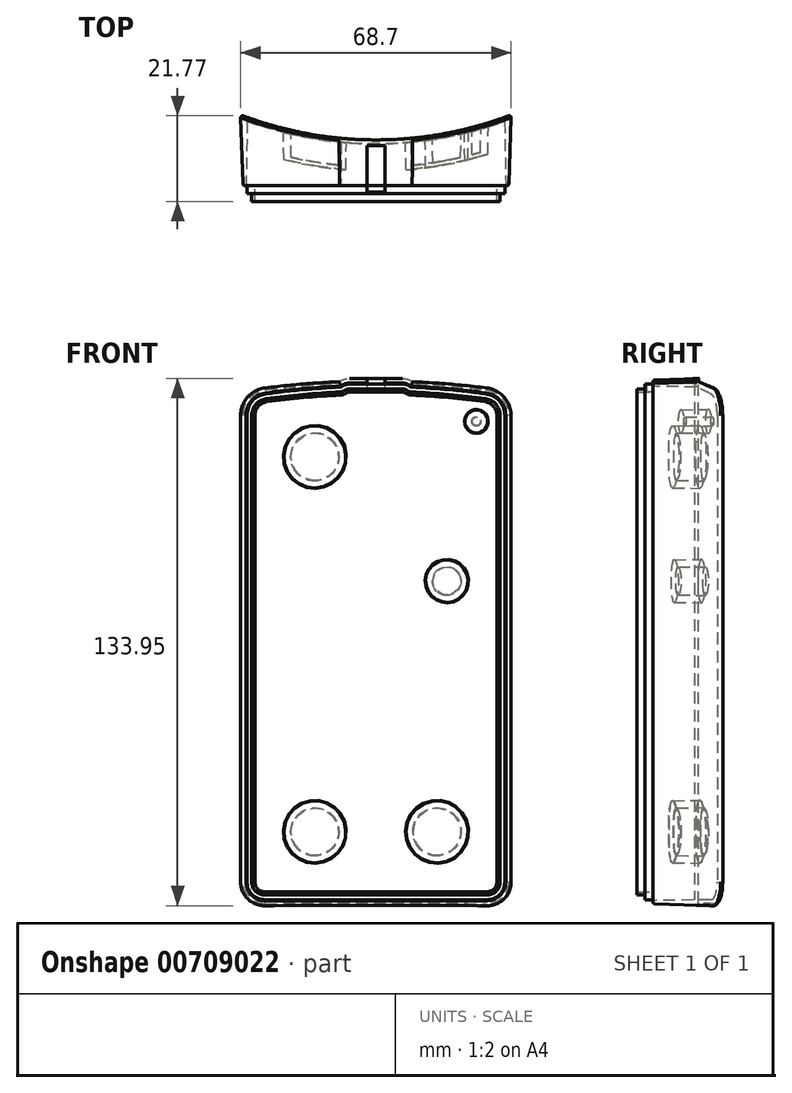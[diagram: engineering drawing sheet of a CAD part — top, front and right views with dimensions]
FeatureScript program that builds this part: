
annotation { "Feature Type Name" : "Feature", "Feature Type Description" : "" }
export const myFeature = defineFeature(function(context is Context, id is Id, definition is map)
    precondition{}
    {
        {
            var Q0;
            Q0=qCreatedBy(makeId("Front.planeOp"),FACE);
            var sketch = newSketch(context, id + "F0", { "sketchPlane" : qUnion([Q0])});
            skLineSegment(sketch, "E0.bottom", {"start": v(4.5, 0) * mm, "end": v(61, 0) * mm});
            skLineSegment(sketch, "E0.left", {"start": v(0, 4.5) * mm, "end": v(0, 123.05) * mm});
            skLineSegment(sketch, "E0.right", {"start": v(65.5, 4.5) * mm, "end": v(65.5, 123.05) * mm});
            skPoint(sketch, "E1.visualSharp", {"position": v(0, 0) * mm});
            skArc(sketch, "E1.filletArc", {"start": v(0, 4.5) * mm, "mid": v(1.32, 1.32) * mm, "end": v(4.5, 0) * mm});
            skPoint(sketch, "E2.visualSharp", {"position": v(65.5, 0) * mm});
            skArc(sketch, "E2.filletArc", {"start": v(61, 0) * mm, "mid": v(64.18, 1.32) * mm, "end": v(65.5, 4.5) * mm});
            skArc(sketch, "E3.filletArc", {"start": v(4.76, 128.5) * mm, "mid": v(1.36, 126.67) * mm, "end": v(0, 123.05) * mm});
            skPoint(sketch, "E4.visualSharp", {"position": v(65.5, 168.18) * mm});
            skArc(sketch, "E4.filletArc", {"start": v(65.5, 123.05) * mm, "mid": v(64.14, 126.67) * mm, "end": v(60.74, 128.5) * mm});
            skArc(sketch, "E5", {"start": v(60.74, 128.5) * mm, "mid": v(51.35, 129.57) * mm, "end": v(41.91, 130.2) * mm});
            skLineSegment(sketch, "E6", {"start": v(26, 131) * mm, "end": v(39.5, 131) * mm});
            skArc(sketch, "E7.trimOffspring", {"start": v(23.59, 130.2) * mm, "mid": v(14.15, 129.57) * mm, "end": v(4.76, 128.5) * mm});
            skLineSegment(sketch, "E8", {"start": v(32.75, 0) * mm, "end": v(32.75, 224.52) * mm, "construction": true});
            skArc(sketch, "E9", {"start": v(26, 131) * mm, "mid": v(25.02, 130.84) * mm, "end": v(24.13, 130.4) * mm});
            skPoint(sketch, "E10.visualSharp", {"position": v(23.91, 130.21) * mm});
            skArc(sketch, "E10.filletArc", {"start": v(23.59, 130.2) * mm, "mid": v(23.87, 130.26) * mm, "end": v(24.13, 130.4) * mm});
            skArc(sketch, "E11.MirrorCS", {"start": v(41.91, 130.2) * mm, "mid": v(41.63, 130.26) * mm, "end": v(41.37, 130.4) * mm});
            skArc(sketch, "E12.MirrorCS", {"start": v(39.5, 131) * mm, "mid": v(40.48, 130.84) * mm, "end": v(41.37, 130.4) * mm});
            skSolve(sketch);
        }
        {
            var Q0;
            Q0=qCreatedBy(makeId("Top.planeOp"),FACE);
            var sketch = newSketch(context, id + "F1", { "sketchPlane" : qUnion([Q0])});
            skArc(sketch, "E13", {"start": v(0, 0) * mm, "mid": v(32.75, -5.75) * mm, "end": v(65.5, 0) * mm});
            skLineSegment(sketch, "E14", {"start": v(0, 0) * mm, "end": v(65.5, 0) * mm});
            skLineSegment(sketch, "E15", {"start": v(0, 0) * mm, "end": v(94.5, 0) * mm, "construction": true});
            skLineSegment(sketch, "E16", {"start": v(94.5, 0) * mm, "end": v(32.75, 0) * mm, "construction": true});
            skLineSegment(sketch, "E17", {"start": v(32.75, 0) * mm, "end": v(32.75, -16.7) * mm, "construction": true});
            skSolve(sketch);
        }
        {
            var Q0;
            Q0=qSketchRegion(id+"F0",true);
            extrude(context, id + "F2", {"entities" : qUnion([Q0]), "depth" : 12.5 * mm, "offsetDistance" : 25 * mm});
        }
        {
            var Q0;
            Q0=qSketchRegion(id+"F1",true);
            extrude(context, id + "F3", {"entities" : qUnion([Q0]), "operationType" : NewBodyOperationType.REMOVE, "endBound" : BoundingType.THROUGH_ALL, "depth" : 25 * mm, "offsetDistance" : 25 * mm});
        }
        {
            var Q0;
            Q0=makeQuery(id+"F2.opExtrude","SWEPT_FACE",FACE,{"disambiguationData":[OSD([sQuery(id+"F0.wireOp",EDGE,"E0.bottom")])]});
            var sketch = newSketch(context, id + "F4", { "sketchPlane" : qUnion([Q0])});
            skLineSegment(sketch, "E18", {"start": v(0, 12.5) * mm, "end": v(0, 10.5) * mm});
            skLineSegment(sketch, "E19", {"start": v(0, 10.5) * mm, "end": v(1.1, 10.5) * mm});
            skLineSegment(sketch, "E20", {"start": v(1.1, 10.5) * mm, "end": v(1.1, 12.5) * mm});
            skLineSegment(sketch, "E21", {"start": v(1.1, 12.5) * mm, "end": v(0, 12.5) * mm});
            skSolve(sketch);
        }
        {
            var Q0;
            Q0=makeQuery(id+"F4.imprint","IMPRINT",FACE,{"disambiguationData":[TD([[makeQuery(id+"F4.imprint","IMPRINT",EDGE,{"derivedFrom":sQuery(id+"F4.wireOp",EDGE,"E18")}),1.0]])]});
            cPlane(context, id + "F5", {"entities" : qUnion([Q0]), "cplaneType" : CPlaneType.OFFSET, "offset" : 50 * mm, "oppositeDirection" : true, "width" : 150 * mm, "height" : 150 * mm});
        }
        {
            var Q0;
            Q0=makeQuery(id+"F2.opExtrude","CAP_FACE",FACE,{"disambiguationData":[OSD([sQuery(id+"F0.wireOp",EDGE,"E0.bottom"),sQuery(id+"F0.wireOp",EDGE,"E0.left"),sQuery(id+"F0.wireOp",EDGE,"E0.right"),sQuery(id+"F0.wireOp",EDGE,"E1.filletArc"),sQuery(id+"F0.wireOp",EDGE,"E2.filletArc"),sQuery(id+"F0.wireOp",EDGE,"E3.filletArc"),sQuery(id+"F0.wireOp",EDGE,"E4.filletArc"),sQuery(id+"F0.wireOp",EDGE,"E5"),sQuery(id+"F0.wireOp",EDGE,"E6"),sQuery(id+"F0.wireOp",EDGE,"4cuLOFSM-Cs9p-uLwk-Nxmp-eiNM5esqOte1"),sQuery(id+"F0.wireOp",EDGE,"qXNs2k06-4niP-ImqC-5Hru-JPzRlnRtqvzY"),sQuery(id+"F0.wireOp",EDGE,"592cab12-c6ad-4f12-8fa5-e9ea6a7a9ab5.filletArc"),sQuery(id+"F0.wireOp",EDGE,"E7.trimOffspring"),sQuery(id+"F0.wireOp",EDGE,"810a662d-7d86-4de4-b075-b749f1e53ed9.filletArc"),sQuery(id+"F0.wireOp",EDGE,"8d541c61-4af1-470d-ac14-312aa46fb37d.filletArc"),sQuery(id+"F0.wireOp",EDGE,"225b199f-dbc8-4900-9de2-33667acb90c7.filletArc")])],"isStart":false});
            shell(context, id + "F6", {"entities" : qUnion([Q0]), "thickness" : 2 * mm});
        }
        {
            var Q0;
            Q0=makeQuery(id+"F2.opExtrude","CAP_FACE",FACE,{"disambiguationData":[OSD([sQuery(id+"F0.wireOp",EDGE,"E0.bottom"),sQuery(id+"F0.wireOp",EDGE,"E0.left"),sQuery(id+"F0.wireOp",EDGE,"E0.right"),sQuery(id+"F0.wireOp",EDGE,"E1.filletArc"),sQuery(id+"F0.wireOp",EDGE,"E2.filletArc"),sQuery(id+"F0.wireOp",EDGE,"E3.filletArc"),sQuery(id+"F0.wireOp",EDGE,"E4.filletArc"),sQuery(id+"F0.wireOp",EDGE,"E5"),sQuery(id+"F0.wireOp",EDGE,"E6"),sQuery(id+"F0.wireOp",EDGE,"E7.trimOffspring"),sQuery(id+"F0.wireOp",EDGE,"E9"),sQuery(id+"F0.wireOp",EDGE,"E10.filletArc"),sQuery(id+"F0.wireOp",EDGE,"E11.MirrorCS"),sQuery(id+"F0.wireOp",EDGE,"E12.MirrorCS")])],"isStart":false});
            var sketch = newSketch(context, id + "F7", { "sketchPlane" : qUnion([Q0])});
            skLineSegment(sketch, "E22.0.0", {"start": v(39.5, 131) * mm, "end": v(26, 131) * mm});
            skArc(sketch, "E22.0.1", {"start": v(26, 131) * mm, "mid": v(25.02, 130.84) * mm, "end": v(24.13, 130.4) * mm});
            skArc(sketch, "E22.0.2", {"start": v(24.13, 130.4) * mm, "mid": v(23.87, 130.26) * mm, "end": v(23.59, 130.2) * mm});
            skArc(sketch, "E22.0.3", {"start": v(23.59, 130.2) * mm, "mid": v(14.15, 129.57) * mm, "end": v(4.76, 128.5) * mm});
            skArc(sketch, "E22.0.4", {"start": v(4.76, 128.5) * mm, "mid": v(1.36, 126.67) * mm, "end": v(0, 123.05) * mm});
            skLineSegment(sketch, "E22.0.5", {"start": v(0, 123.05) * mm, "end": v(0, 4.5) * mm});
            skArc(sketch, "E22.0.6", {"start": v(0, 4.5) * mm, "mid": v(1.32, 1.32) * mm, "end": v(4.5, 0) * mm});
            skLineSegment(sketch, "E22.0.7", {"start": v(4.5, 0) * mm, "end": v(61, 0) * mm});
            skArc(sketch, "E22.0.8", {"start": v(61, 0) * mm, "mid": v(64.18, 1.32) * mm, "end": v(65.5, 4.5) * mm});
            skLineSegment(sketch, "E22.0.9", {"start": v(65.5, 4.5) * mm, "end": v(65.5, 123.05) * mm});
            skArc(sketch, "E22.0.10", {"start": v(65.5, 123.05) * mm, "mid": v(64.14, 126.67) * mm, "end": v(60.74, 128.5) * mm});
            skArc(sketch, "E22.0.11", {"start": v(60.74, 128.5) * mm, "mid": v(51.35, 129.57) * mm, "end": v(41.91, 130.2) * mm});
            skArc(sketch, "E22.0.12", {"start": v(41.91, 130.2) * mm, "mid": v(41.63, 130.26) * mm, "end": v(41.37, 130.4) * mm});
            skArc(sketch, "E22.0.13", {"start": v(41.37, 130.4) * mm, "mid": v(40.48, 130.84) * mm, "end": v(39.5, 131) * mm});
            skArc(sketch, "E23.0", {"start": v(40.66, 129.42) * mm, "mid": v(40.1, 129.7) * mm, "end": v(39.5, 129.8) * mm});
            skArc(sketch, "E23.1", {"start": v(41.86, 129) * mm, "mid": v(41.23, 129.12) * mm, "end": v(40.66, 129.42) * mm});
            skArc(sketch, "E23.2", {"start": v(60.58, 127.31) * mm, "mid": v(51.24, 128.37) * mm, "end": v(41.86, 129) * mm});
            skArc(sketch, "E23.3", {"start": v(4.92, 127.31) * mm, "mid": v(2.26, 125.88) * mm, "end": v(1.2, 123.05) * mm});
            skArc(sketch, "E23.4", {"start": v(23.64, 129) * mm, "mid": v(14.26, 128.37) * mm, "end": v(4.92, 127.31) * mm});
            skArc(sketch, "E23.5", {"start": v(24.84, 129.42) * mm, "mid": v(24.27, 129.12) * mm, "end": v(23.64, 129) * mm});
            skArc(sketch, "E23.6", {"start": v(26, 129.8) * mm, "mid": v(25.4, 129.7) * mm, "end": v(24.84, 129.42) * mm});
            skLineSegment(sketch, "E23.7", {"start": v(1.2, 123.05) * mm, "end": v(1.2, 4.5) * mm});
            skArc(sketch, "E23.8", {"start": v(1.2, 4.5) * mm, "mid": v(2.17, 2.17) * mm, "end": v(4.5, 1.2) * mm});
            skLineSegment(sketch, "E23.9", {"start": v(4.5, 1.2) * mm, "end": v(61, 1.2) * mm});
            skLineSegment(sketch, "E23.10", {"start": v(39.5, 129.8) * mm, "end": v(26, 129.8) * mm});
            skArc(sketch, "E23.11", {"start": v(61, 1.2) * mm, "mid": v(63.33, 2.17) * mm, "end": v(64.3, 4.5) * mm});
            skLineSegment(sketch, "E23.12", {"start": v(64.3, 4.5) * mm, "end": v(64.3, 123.05) * mm});
            skArc(sketch, "E23.13", {"start": v(64.3, 123.05) * mm, "mid": v(63.24, 125.88) * mm, "end": v(60.58, 127.31) * mm});
            skSolve(sketch);
        }
        {
            var Q0;
            Q0=qSketchRegion(id+"F7",true);
            extrude(context, id + "F8", {"entities" : qUnion([Q0]), "operationType" : NewBodyOperationType.REMOVE, "oppositeDirection" : true, "depth" : 2 * mm, "offsetDistance" : 25 * mm});
        }
        {
            var Q0;
            Q0=makeQuery(id+"F6.opShell","OFFSET_EDGE",EDGE,{"disambiguationData":[OSD([sQuery(id+"F0.wireOp",EDGE,"E7.trimOffspring")])]});
            var Q1;
            Q1=makeQuery(id+"F8.boolean.opBoolean","COPY",EDGE,{"derivedFrom":makeQuery(id+"F8.opExtrude","CAP_EDGE",EDGE,{"disambiguationData":[OSD([sQuery(id+"F7.wireOp",EDGE,"E23.4")])],"isStart":true})});
            fillet(context, id + "F9", {"entities" : qUnion([Q0, Q1]), "radius" : .2 * mm, "tangentPropagation" : true, "allowEdgeOverflow" : false});
        }
        {
            var Q0;
            Q0=qCreatedBy(makeId("Front.planeOp"),FACE);
            var sketch = newSketch(context, id + "F10", { "sketchPlane" : qUnion([Q0])});
            skCircle(sketch, "E24", {"center": v(52.88, 68) * mm, "radius": 5.12 * mm});
            skArc(sketch, "E25", {"start": v(16.47, 64.05) * mm, "mid": v(12.44, 73) * mm, "end": v(9.49, 63.64) * mm});
            skArc(sketch, "E26", {"start": v(10.62, 44.32) * mm, "mid": v(14.94, 30.41) * mm, "end": v(17.6, 44.73) * mm});
            skLineSegment(sketch, "E27", {"start": v(12.75, 67.75) * mm, "end": v(14.5, 37.9) * mm, "construction": true});
            skLineSegment(sketch, "E28", {"start": v(16.47, 64.05) * mm, "end": v(17.6, 44.73) * mm});
            skLineSegment(sketch, "E29.MirrorCS", {"start": v(9.49, 63.64) * mm, "end": v(10.62, 44.32) * mm});
            skSolve(sketch);
        }
        {
            var Q0;
            Q0=qSketchRegion(id+"F10",true);
            extrude(context, id + "F11", {"entities" : qUnion([Q0]), "operationType" : NewBodyOperationType.REMOVE, "endBound" : BoundingType.THROUGH_ALL, "depth" : 25 * mm, "offsetDistance" : 25 * mm});
        }
        {
            var Q0;
            Q0=qCreatedBy(makeId("Front.planeOp"),FACE);
            var sketch = newSketch(context, id + "F12", { "sketchPlane" : qUnion([Q0])});
            skLineSegment(sketch, "E30", {"start": v(51.75, 114.46) * mm, "end": v(32.54, 67.75) * mm, "construction": true});
            skArc(sketch, "E31.0.startCap", {"start": v(49.2, 115.5) * mm, "mid": v(52.8, 117) * mm, "end": v(54.3, 113.41) * mm});
            skArc(sketch, "E31.0.endCap", {"start": v(35.09, 66.7) * mm, "mid": v(31.5, 65.2) * mm, "end": v(30, 68.8) * mm});
            skLineSegment(sketch, "E31.0.left", {"start": v(54.3, 113.41) * mm, "end": v(35.09, 66.7) * mm});
            skLineSegment(sketch, "E31.0.right", {"start": v(49.2, 115.5) * mm, "end": v(30, 68.8) * mm});
            skLineSegment(sketch, "E32.0", {"start": v(48.28, 115.89) * mm, "end": v(29.08, 69.18) * mm});
            skArc(sketch, "E32.1", {"start": v(48.28, 115.89) * mm, "mid": v(53.18, 117.93) * mm, "end": v(55.22, 113.03) * mm});
            skLineSegment(sketch, "E32.2", {"start": v(55.22, 113.03) * mm, "end": v(36.01, 66.32) * mm});
            skArc(sketch, "E32.3", {"start": v(36.01, 66.32) * mm, "mid": v(31.12, 64.28) * mm, "end": v(29.08, 69.18) * mm});
            skSolve(sketch);
        }
        {
            var Q0;
            {var subQ0=sQuery(id+"F1.wireOp",EDGE,"E14");var subQ1=sQuery(id+"F1.wireOp",EDGE,"E13");Q0=makeQuery(id+"F3.boolean.opBoolean","MERGE",EDGE,{"derivedFrom":[makeQuery(id+"F2.opExtrude","CAP_EDGE",EDGE,{"disambiguationData":[OSD([sQuery(id+"F0.wireOp",EDGE,"E0.left")])],"isStart":true}),makeQuery(id+"F3.opExtrude","SWEPT_EDGE",EDGE,{"disambiguationData":[OSD([subQ1,subQ0]),TDD([makeQuery(id+"F1.imprint","INTERSECT",VERTEX,{"disambiguationData":[OD(0.0)],"derivedFrom":[subQ1,subQ0]})])]})]});}
            fillet(context, id + "F13", {"entities" : qUnion([Q0]), "radius" : .5 * mm, "tangentPropagation" : true, "allowEdgeOverflow" : false});
        }
        {
            var Q0;
            Q0=qSketchRegion(id+"F12",true);
            var Q1;
            Q1=makeQuery(id+"F3.boolean.opBoolean","COPY",FACE,{"derivedFrom":makeQuery(id+"F3.opExtrude","SWEPT_FACE",FACE,{"disambiguationData":[OSD([sQuery(id+"F1.wireOp",EDGE,"E13")])]})});
            var Q2;
            Q2=makeQuery(id+"F2.opExtrude","SWEPT_BODY",BODY,{"disambiguationData":[OSD([sQuery(id+"F0.wireOp",EDGE,"E0.bottom"),sQuery(id+"F0.wireOp",EDGE,"E0.left"),sQuery(id+"F0.wireOp",EDGE,"E0.right"),sQuery(id+"F0.wireOp",EDGE,"E1.filletArc"),sQuery(id+"F0.wireOp",EDGE,"E2.filletArc"),sQuery(id+"F0.wireOp",EDGE,"E3.filletArc"),sQuery(id+"F0.wireOp",EDGE,"E4.filletArc"),sQuery(id+"F0.wireOp",EDGE,"E5"),sQuery(id+"F0.wireOp",EDGE,"E6"),sQuery(id+"F0.wireOp",EDGE,"E7.trimOffspring"),sQuery(id+"F0.wireOp",EDGE,"E9"),sQuery(id+"F0.wireOp",EDGE,"E10.filletArc"),sQuery(id+"F0.wireOp",EDGE,"E11.MirrorCS"),sQuery(id+"F0.wireOp",EDGE,"E12.MirrorCS")])]});
            var Q3;
            Q3=makeQuery(id+"F3.boolean.opBoolean","COPY",FACE,{"derivedFrom":makeQuery(id+"F3.opExtrude","SWEPT_FACE",FACE,{"disambiguationData":[OSD([sQuery(id+"F1.wireOp",EDGE,"E13")])]})});
            extrude(context, id + "F14", {"entities" : qUnion([Q0]), "operationType" : NewBodyOperationType.ADD, "endBound" : BoundingType.UP_TO_SURFACE, "depth" : 25 * mm, "endBoundEntityFace" : qUnion([Q1]), "endBoundEntityBody" : qUnion([Q2]), "offsetDistance" : 1 * mm, "offsetOppositeDirection" : true, "hasSecondDirection" : true, "secondDirectionBound" : BoundingType.UP_TO_SURFACE, "secondDirectionOppositeDirection" : false, "secondDirectionDepth" : 1 * mm, "secondDirectionBoundEntityFace" : qUnion([Q3]), "hasSecondDirectionOffset" : true, "secondDirectionOffsetDistance" : .5 * mm});
        }
        {
            var Q0;
            Q0=makeQuery(id+"F14.opExtrude","CAP_EDGE",EDGE,{"disambiguationData":[OSD([sQuery(id+"F12.wireOp",EDGE,"E31.0.left")])],"isStart":true});
            var Q1;
            Q1=makeQuery(id+"F14.opExtrude","CAP_EDGE",EDGE,{"disambiguationData":[OSD([sQuery(id+"F12.wireOp",EDGE,"E32.2")])],"isStart":true});
            fillet(context, id + "F15", {"entities" : qUnion([Q0, Q1]), "radius" : .5 * mm, "tangentPropagation" : true, "allowEdgeOverflow" : false});
        }
        {
            var Q0;
            Q0=qCreatedBy(makeId("Front.planeOp"),FACE);
            var sketch = newSketch(context, id + "F16", { "sketchPlane" : qUnion([Q0])});
            skCircle(sketch, "E33", {"center": v(51.75, 114.46) * mm, "radius": 0.75 * mm});
            skLineSegment(sketch, "E34.0", {"start": v(51.75, 114.46) * mm, "end": v(32.54, 67.75) * mm, "construction": true});
            skSolve(sketch);
        }
        {
            var Q0;
            Q0=makeQuery(id+"F16.imprint","IMPRINT",FACE,{"disambiguationData":[TD([[makeQuery(id+"F16.imprint","IMPRINT",EDGE,{"derivedFrom":sQuery(id+"F16.wireOp",EDGE,"E33")}),1.0]])]});
            var Q1;
            Q1=qConstructionFilter(qBodyType(qCreatedBy(id+"F16",EDGE),BodyType.WIRE),ConstructionObject.NO);
            extrude(context, id + "F17", {"entities" : qUnion([Q0]), "operationType" : NewBodyOperationType.REMOVE, "surfaceEntities" : qUnion([Q1]), "endBound" : BoundingType.THROUGH_ALL, "depth" : 25 * mm, "offsetDistance" : 25 * mm});
        }
        {
            var Q0;
            Q0=qCreatedBy(makeId("Top.planeOp"),FACE);
            var sketch = newSketch(context, id + "F18", { "sketchPlane" : qUnion([Q0])});
            skLineSegment(sketch, "E35.0", {"start": v(-0.5, -7.5) * mm, "end": v(-0.5, 1.21) * mm});
            skLineSegment(sketch, "E35.1", {"start": v(66, -7.57) * mm, "end": v(66, 1.14) * mm});
            skLineSegment(sketch, "E36", {"start": v(32.75, -4) * mm, "end": v(32.75, 0.99) * mm, "construction": true});
            skPoint(sketch, "E36.startSnap0", {"position": v(32.75, -4) * mm});
            skArc(sketch, "E37.0", {"start": v(66, 1.14) * mm, "mid": v(32.75, -4.75) * mm, "end": v(-0.5, 1.21) * mm});
            skSolve(sketch);
        }
        {
            var Q0;
            Q0=makeQuery(id+"F8.boolean.opBoolean","COPY",FACE,{"derivedFrom":makeQuery(id+"F8.opExtrude","CAP_FACE",FACE,{"disambiguationData":[OSD([sQuery(id+"F7.wireOp",EDGE,"E22.0.0"),sQuery(id+"F7.wireOp",EDGE,"E22.0.1"),sQuery(id+"F7.wireOp",EDGE,"E22.0.2"),sQuery(id+"F7.wireOp",EDGE,"E22.0.3"),sQuery(id+"F7.wireOp",EDGE,"E22.0.4"),sQuery(id+"F7.wireOp",EDGE,"E22.0.5"),sQuery(id+"F7.wireOp",EDGE,"E22.0.6"),sQuery(id+"F7.wireOp",EDGE,"E22.0.7"),sQuery(id+"F7.wireOp",EDGE,"E22.0.8"),sQuery(id+"F7.wireOp",EDGE,"E22.0.9"),sQuery(id+"F7.wireOp",EDGE,"E22.0.10"),sQuery(id+"F7.wireOp",EDGE,"E22.0.11"),sQuery(id+"F7.wireOp",EDGE,"E22.0.12"),sQuery(id+"F7.wireOp",EDGE,"E22.0.13"),sQuery(id+"F7.wireOp",EDGE,"E23.0"),sQuery(id+"F7.wireOp",EDGE,"E23.1"),sQuery(id+"F7.wireOp",EDGE,"E23.2"),sQuery(id+"F7.wireOp",EDGE,"E23.3"),sQuery(id+"F7.wireOp",EDGE,"E23.4"),sQuery(id+"F7.wireOp",EDGE,"E23.5"),sQuery(id+"F7.wireOp",EDGE,"E23.6"),sQuery(id+"F7.wireOp",EDGE,"E23.7"),sQuery(id+"F7.wireOp",EDGE,"E23.8"),sQuery(id+"F7.wireOp",EDGE,"E23.9"),sQuery(id+"F7.wireOp",EDGE,"E23.10"),sQuery(id+"F7.wireOp",EDGE,"E23.11"),sQuery(id+"F7.wireOp",EDGE,"E23.12"),sQuery(id+"F7.wireOp",EDGE,"E23.13")])],"isStart":false})});
            cPlane(context, id + "F19", {"entities" : qUnion([Q0]), "cplaneType" : CPlaneType.OFFSET, "offset" : 2 * mm, "oppositeDirection" : true, "width" : 150 * mm, "height" : 150 * mm});
        }
        {
            var Q0;
            Q0=qCreatedBy(id+"F19.planeOp",FACE);
            var sketch = newSketch(context, id + "F20", { "sketchPlane" : qUnion([Q0])});
            skLineSegment(sketch, "E38.0.0", {"start": v(39.5, 131) * mm, "end": v(26, 131) * mm});
            skArc(sketch, "E38.0.1", {"start": v(26, 131) * mm, "mid": v(25.02, 130.84) * mm, "end": v(24.13, 130.4) * mm});
            skArc(sketch, "E38.0.2", {"start": v(24.13, 130.4) * mm, "mid": v(23.87, 130.26) * mm, "end": v(23.59, 130.2) * mm});
            skArc(sketch, "E38.0.3", {"start": v(23.59, 130.2) * mm, "mid": v(14.15, 129.57) * mm, "end": v(4.76, 128.5) * mm});
            skArc(sketch, "E38.0.4", {"start": v(4.76, 128.5) * mm, "mid": v(1.36, 126.67) * mm, "end": v(0, 123.05) * mm});
            skLineSegment(sketch, "E38.0.5", {"start": v(0, 123.05) * mm, "end": v(0, 4.5) * mm});
            skArc(sketch, "E38.0.6", {"start": v(0, 4.5) * mm, "mid": v(1.32, 1.32) * mm, "end": v(4.5, 0) * mm});
            skLineSegment(sketch, "E38.0.7", {"start": v(4.5, 0) * mm, "end": v(61, 0) * mm});
            skArc(sketch, "E38.0.8", {"start": v(61, 0) * mm, "mid": v(64.18, 1.32) * mm, "end": v(65.5, 4.5) * mm});
            skLineSegment(sketch, "E38.0.9", {"start": v(65.5, 4.5) * mm, "end": v(65.5, 123.05) * mm});
            skArc(sketch, "E38.0.10", {"start": v(65.5, 123.05) * mm, "mid": v(64.14, 126.67) * mm, "end": v(60.74, 128.5) * mm});
            skArc(sketch, "E38.0.11", {"start": v(60.74, 128.5) * mm, "mid": v(51.35, 129.57) * mm, "end": v(41.91, 130.2) * mm});
            skArc(sketch, "E38.0.12", {"start": v(41.91, 130.2) * mm, "mid": v(41.63, 130.26) * mm, "end": v(41.37, 130.4) * mm});
            skArc(sketch, "E38.0.13", {"start": v(41.37, 130.4) * mm, "mid": v(40.48, 130.84) * mm, "end": v(39.5, 131) * mm});
            skLineSegment(sketch, "E39.0", {"start": v(4.5, -1) * mm, "end": v(61, -1) * mm});
            skArc(sketch, "E39.1", {"start": v(41.96, 131.2) * mm, "mid": v(40.8, 131.8) * mm, "end": v(39.5, 132) * mm});
            skArc(sketch, "E39.2", {"start": v(60.88, 129.5) * mm, "mid": v(51.44, 130.56) * mm, "end": v(41.96, 131.2) * mm});
            skArc(sketch, "E39.3", {"start": v(66.5, 123.05) * mm, "mid": v(64.9, 127.32) * mm, "end": v(60.88, 129.5) * mm});
            skLineSegment(sketch, "E39.4", {"start": v(66.5, 4.5) * mm, "end": v(66.5, 123.05) * mm});
            skLineSegment(sketch, "E39.5", {"start": v(39.5, 132) * mm, "end": v(26, 132) * mm});
            skArc(sketch, "E39.6", {"start": v(61, -1) * mm, "mid": v(64.89, 0.61) * mm, "end": v(66.5, 4.5) * mm});
            skArc(sketch, "E39.7", {"start": v(26, 132) * mm, "mid": v(24.7, 131.8) * mm, "end": v(23.54, 131.2) * mm});
            skArc(sketch, "E39.8", {"start": v(23.54, 131.2) * mm, "mid": v(14.06, 130.56) * mm, "end": v(4.62, 129.5) * mm});
            skArc(sketch, "E39.9", {"start": v(4.62, 129.5) * mm, "mid": v(0.6, 127.32) * mm, "end": v(-1, 123.05) * mm});
            skLineSegment(sketch, "E39.10", {"start": v(-1, 123.05) * mm, "end": v(-1, 4.5) * mm});
            skArc(sketch, "E39.11", {"start": v(-1, 4.5) * mm, "mid": v(0.61, 0.61) * mm, "end": v(4.5, -1) * mm});
            skArc(sketch, "E40.0", {"start": v(4.72, 128.75) * mm, "mid": v(1.17, 126.83) * mm, "end": v(-0.25, 123.05) * mm});
            skLineSegment(sketch, "E40.1", {"start": v(65.75, 4.5) * mm, "end": v(65.75, 123.05) * mm});
            skArc(sketch, "E40.2", {"start": v(61, -0.25) * mm, "mid": v(64.36, 1.14) * mm, "end": v(65.75, 4.5) * mm});
            skLineSegment(sketch, "E40.3", {"start": v(4.5, -0.25) * mm, "end": v(61, -0.25) * mm});
            skArc(sketch, "E40.4", {"start": v(-0.25, 4.5) * mm, "mid": v(1.14, 1.14) * mm, "end": v(4.5, -0.25) * mm});
            skArc(sketch, "E40.5", {"start": v(65.75, 123.05) * mm, "mid": v(64.33, 126.83) * mm, "end": v(60.78, 128.75) * mm});
            skLineSegment(sketch, "E40.6", {"start": v(-0.25, 123.05) * mm, "end": v(-0.25, 4.5) * mm});
            skArc(sketch, "E40.7", {"start": v(60.78, 128.75) * mm, "mid": v(51.25, 129.82) * mm, "end": v(41.68, 130.46) * mm});
            skArc(sketch, "E40.8", {"start": v(41.68, 130.46) * mm, "mid": v(40.66, 131.05) * mm, "end": v(39.5, 131.25) * mm});
            skLineSegment(sketch, "E40.9", {"start": v(39.5, 131.25) * mm, "end": v(26, 131.25) * mm});
            skArc(sketch, "E40.10", {"start": v(26, 131.25) * mm, "mid": v(24.84, 131.05) * mm, "end": v(23.82, 130.46) * mm});
            skArc(sketch, "E40.11", {"start": v(23.82, 130.46) * mm, "mid": v(14.25, 129.82) * mm, "end": v(4.72, 128.75) * mm});
            skSolve(sketch);
        }
        {
            var Q0;
            Q0=makeQuery(id+"F20.imprint","IMPRINT",FACE,{"disambiguationData":[TD([[makeQuery(id+"F20.imprint","IMPRINT",EDGE,{"derivedFrom":sQuery(id+"F20.wireOp",EDGE,"E38.0.0")}),-1.0]])]});
            var Q1;
            Q1=makeQuery(id+"F20.imprint","IMPRINT",FACE,{"disambiguationData":[TD([[makeQuery(id+"F20.imprint","IMPRINT",EDGE,{"derivedFrom":sQuery(id+"F20.wireOp",EDGE,"E38.0.0")}),1.0]])]});
            var Q2;
            Q2=makeQuery(id+"F20.imprint","IMPRINT",FACE,{"disambiguationData":[TD([[makeQuery(id+"F20.imprint","IMPRINT",EDGE,{"derivedFrom":sQuery(id+"F20.wireOp",EDGE,"E39.0")}),1.0]])]});
            extrude(context, id + "F21", {"entities" : qUnion([Q0, Q1, Q2]), "oppositeDirection" : true, "depth" : 18 * mm, "offsetDistance" : 25 * mm, "hasDraft" : true, "draftAngle" : 2 * degree});
        }
        {
            var Q0;
            Q0=qCreatedBy(makeId("Top.planeOp"),FACE);
            var sketch = newSketch(context, id + "F22", { "sketchPlane" : qUnion([Q0])});
            skLineSegment(sketch, "E41.0.0", {"start": v(61, -8.5) * mm, "end": v(4.5, -8.5) * mm, "construction": true});
            skLineSegment(sketch, "E41.0.1", {"start": v(4.5, 9.5) * mm, "end": v(4.5, -8.5) * mm, "construction": true});
            skLineSegment(sketch, "E41.0.2", {"start": v(4.5, 9.5) * mm, "end": v(61, 9.5) * mm, "construction": true});
            skLineSegment(sketch, "E41.0.3", {"start": v(61, 9.5) * mm, "end": v(61, -8.5) * mm, "construction": true});
            skLineSegment(sketch, "E41.1.0", {"start": v(66.5, -8.5) * mm, "end": v(61, -8.5) * mm, "construction": true});
            skLineSegment(sketch, "E41.1.1", {"start": v(61, 9.5) * mm, "end": v(61, -8.5) * mm, "construction": true});
            skLineSegment(sketch, "E41.1.2", {"start": v(61, 9.5) * mm, "end": v(67.13, 9.5) * mm, "construction": true});
            skLineSegment(sketch, "E41.1.3", {"start": v(67.13, 9.5) * mm, "end": v(66.5, -8.5) * mm, "construction": true});
            skLineSegment(sketch, "E41.2.0", {"start": v(4.5, -8.5) * mm, "end": v(-1, -8.5) * mm, "construction": true});
            skLineSegment(sketch, "E41.2.1", {"start": v(-1.63, 9.5) * mm, "end": v(-1, -8.5) * mm, "construction": true});
            skLineSegment(sketch, "E41.2.2", {"start": v(-1.63, 9.5) * mm, "end": v(4.5, 9.5) * mm, "construction": true});
            skLineSegment(sketch, "E41.2.3", {"start": v(4.5, 9.5) * mm, "end": v(4.5, -8.5) * mm, "construction": true});
            skArc(sketch, "E42", {"start": v(-1.63, 9.5) * mm, "mid": v(32.75, 3.14) * mm, "end": v(67.13, 9.5) * mm});
            skLineSegment(sketch, "E43", {"start": v(-1.63, 9.5) * mm, "end": v(67.13, 9.5) * mm});
            skSolve(sketch);
        }
        {
            var Q0;
            Q0=makeQuery(id+"F22.imprint","IMPRINT",FACE,{"disambiguationData":[TD([[makeQuery(id+"F22.imprint","IMPRINT",EDGE,{"derivedFrom":sQuery(id+"F22.wireOp",EDGE,"E42")}),1.0]])]});
            extrude(context, id + "F23", {"entities" : qUnion([Q0]), "operationType" : NewBodyOperationType.REMOVE, "endBound" : BoundingType.THROUGH_ALL, "oppositeDirection" : true, "depth" : 25 * mm, "offsetDistance" : 25 * mm, "hasSecondDirection" : true, "secondDirectionBound" : BoundingType.THROUGH_ALL, "secondDirectionOppositeDirection" : false, "secondDirectionDepth" : 25 * mm});
        }
        {
            var Q0;
            Q0=qCreatedBy(makeId("Top.planeOp"),FACE);
            cPlane(context, id + "F24", {"entities" : qUnion([Q0]), "cplaneType" : CPlaneType.OFFSET, "offset" : 6.5 * mm, "oppositeDirection" : true, "width" : 150 * mm, "height" : 150 * mm});
        }
        {
            var Q0;
            Q0=sQuery(id+"F18.wireOp",EDGE,"E37.0");
            extrude(context, id + "F25", {"bodyType" : ToolBodyType.SURFACE, "surfaceEntities" : qUnion([Q0]), "oppositeDirection" : true, "depth" : 5 * mm, "offsetDistance" : 25 * mm, "hasSecondDirection" : true, "secondDirectionOppositeDirection" : false, "secondDirectionDepth" : 150 * mm});
        }
        {
            var Q0;
            Q0=qCreatedBy(id+"F24.planeOp",FACE);
            var sketch = newSketch(context, id + "F26", { "sketchPlane" : qUnion([Q0])});
            skArc(sketch, "E44.0", {"start": v(-0.75, 1.9) * mm, "mid": v(32.75, -4.13) * mm, "end": v(66.25, 1.9) * mm});
            skLineSegment(sketch, "E45.0.0", {"start": v(39.5, -10.5) * mm, "end": v(39.5, -6.01) * mm, "construction": true});
            skArc(sketch, "E45.0.1", {"start": v(39.5, -6.01) * mm, "mid": v(32.75, -6.25) * mm, "end": v(26, -6.01) * mm, "construction": true});
            skLineSegment(sketch, "E45.0.2", {"start": v(26, -6.01) * mm, "end": v(26, -10.5) * mm, "construction": true});
            skLineSegment(sketch, "E45.0.3", {"start": v(26, -10.5) * mm, "end": v(39.5, -10.5) * mm, "construction": true});
            skLineSegment(sketch, "E46", {"start": v(32.75, -10.5) * mm, "end": v(32.75, 21.11) * mm, "construction": true});
            skPoint(sketch, "E46.endSnap0", {"position": v(32.75, -6.25) * mm});
            skSolve(sketch);
        }
        {
            var Q0;
            Q0=sQuery(id+"F26.wireOp",EDGE,"E44.0");
            extrude(context, id + "F27", {"bodyType" : ToolBodyType.SURFACE, "surfaceEntities" : qUnion([Q0]), "depth" : 147.2 * mm, "offsetDistance" : 25 * mm});
        }
        {
            var Q0;
            Q0=qCreatedBy(makeId("Front.planeOp"),FACE);
            cPlane(context, id + "F28", {"entities" : qUnion([Q0]), "cplaneType" : CPlaneType.OFFSET, "offset" : 10 * mm, "oppositeDirection" : true, "width" : 150 * mm, "height" : 150 * mm});
        }
        {
            var Q0;
            Q0=sQuery(id+"F22.wireOp",EDGE,"E42");
            extrude(context, id + "F29", {"bodyType" : ToolBodyType.SURFACE, "surfaceEntities" : qUnion([Q0]), "oppositeDirection" : true, "depth" : 10 * mm, "offsetDistance" : 25 * mm, "hasSecondDirection" : true, "secondDirectionOppositeDirection" : false, "secondDirectionDepth" : 141.6 * mm});
        }
        {
            var Q0;
            Q0=makeQuery(id+"F29.opExtrude","SWEPT_BODY",BODY,{"disambiguationData":[OSD([sQuery(id+"F22.wireOp",EDGE,"E42")])]});
            transform(context, id + "F30", {"entities" : qUnion([Q0]), "transformType" : TransformType.TRANSLATION_3D, "dx" : 0 * mm, "dy" : -1 * mm, "dz" : 0 * mm, "makeCopy" : false});
        }
        {
            var Q0;
            Q0=qCreatedBy(makeId("Top.planeOp"),FACE);
            cPlane(context, id + "F31", {"entities" : qUnion([Q0]), "cplaneType" : CPlaneType.OFFSET, "offset" : 140.2 * mm, "width" : 150 * mm, "height" : 150 * mm});
        }
        {
            var Q0;
            Q0=qCreatedBy(id+"F31.planeOp",FACE);
            var sketch = newSketch(context, id + "F32", { "sketchPlane" : qUnion([Q0])});
            skLineSegment(sketch, "E47.0.0", {"start": v(26, 3.38) * mm, "end": v(26, -6.5) * mm, "construction": true});
            skLineSegment(sketch, "E47.0.1", {"start": v(26, -6.5) * mm, "end": v(39.5, -6.5) * mm, "construction": true});
            skLineSegment(sketch, "E47.0.2", {"start": v(39.5, 3.38) * mm, "end": v(39.5, -6.5) * mm, "construction": true});
            skArc(sketch, "E47.0.3", {"start": v(36, 3.2) * mm, "mid": v(32.75, 3.14) * mm, "end": v(29.5, 3.2) * mm});
            skLineSegment(sketch, "E48", {"start": v(32.75, -6.5) * mm, "end": v(32.75, 3.14) * mm, "construction": true});
            skLineSegment(sketch, "E49", {"start": v(29.5, 3.2) * mm, "end": v(29.5, -0.1) * mm});
            skLineSegment(sketch, "E50.MirrorCS", {"start": v(36, 3.2) * mm, "end": v(36, -0.1) * mm});
            skArc(sketch, "E51", {"start": v(29.5, -0.1) * mm, "mid": v(32.75, -3.36) * mm, "end": v(36, -0.1) * mm});
            skSolve(sketch);
        }
        {
            var Q0;
            Q0=makeQuery(id+"F21.opExtrude","CAP_EDGE",EDGE,{"disambiguationData":[OSD([sQuery(id+"F20.wireOp",EDGE,"E39.2")])],"isStart":true});
            var Q1;
            Q1=makeQuery(id+"F21.opExtrude","CAP_EDGE",EDGE,{"disambiguationData":[OSD([sQuery(id+"F20.wireOp",EDGE,"E39.1")])],"isStart":true});
            fillet(context, id + "F33", {"entities" : qUnion([Q0, Q1]), "radius" : .5 * mm, "tangentPropagation" : true, "allowEdgeOverflow" : false});
        }
        {
            var Q0;
            Q0=qCreatedBy(makeId("Front.planeOp"),FACE);
            var sketch = newSketch(context, id + "F34", { "sketchPlane" : qUnion([Q0])});
            skArc(sketch, "E52.0", {"start": v(36, 115.24) * mm, "mid": v(32.75, 115.26) * mm, "end": v(29.5, 115.24) * mm});
            skArc(sketch, "E53", {"start": v(29.5, 115.24) * mm, "mid": v(32.75, 112.01) * mm, "end": v(36, 115.24) * mm});
            skSolve(sketch);
        }
        {
            var Q0;
            Q0=makeQuery(id+"F20.imprint","IMPRINT",FACE,{"disambiguationData":[TD([[makeQuery(id+"F20.imprint","IMPRINT",EDGE,{"derivedFrom":sQuery(id+"F20.wireOp",EDGE,"E38.0.0")}),-1.0]])]});
            var Q1;
            Q1=makeQuery(id+"F20.imprint","IMPRINT",FACE,{"disambiguationData":[TD([[makeQuery(id+"F20.imprint","IMPRINT",EDGE,{"derivedFrom":sQuery(id+"F20.wireOp",EDGE,"E38.0.0")}),1.0]])]});
            var Q2;
            Q2=makeQuery(id+"F29.opExtrude","SWEPT_FACE",FACE,{"disambiguationData":[OSD([sQuery(id+"F22.wireOp",EDGE,"E42")])]});
            extrude(context, id + "F35", {"entities" : qUnion([Q0, Q1]), "operationType" : NewBodyOperationType.REMOVE, "endBound" : BoundingType.UP_TO_SURFACE, "oppositeDirection" : true, "depth" : 25 * mm, "endBoundEntityFace" : qUnion([Q2]), "offsetDistance" : 25 * mm, "hasDraft" : true, "draftAngle" : 1 * degree, "draftPullDirection" : true});
        }
        {
            var Q0;
            Q0=qCreatedBy(makeId("Front.planeOp"),FACE);
            cPlane(context, id + "F36", {"entities" : qUnion([Q0]), "cplaneType" : CPlaneType.OFFSET, "offset" : 25 * mm, "width" : 150 * mm, "height" : 150 * mm});
        }
        {
            var Q0;
            Q0=qCreatedBy(id+"F36.planeOp",FACE);
            var sketch = newSketch(context, id + "F37", { "sketchPlane" : qUnion([Q0])});
            skCircle(sketch, "E54", {"center": v(48.25, 17.25) * mm, "radius": 7.5 * mm});
            skLineSegment(sketch, "E55.0", {"start": v(4.5, -0.52) * mm, "end": v(61, -0.52) * mm, "construction": true});
            skLineSegment(sketch, "E56", {"start": v(32.75, -0.52) * mm, "end": v(32.75, 50.45) * mm, "construction": true});
            skCircle(sketch, "E57.MirrorC", {"center": v(17.25, 17.25) * mm, "radius": 7.5 * mm});
            skCircle(sketch, "E58.MirrorC", {"center": v(17.25, 112.52) * mm, "radius": 7.5 * mm});
            skCircle(sketch, "E59", {"center": v(50.75, 80.95) * mm, "radius": 5 * mm});
            skCircle(sketch, "E60", {"center": v(58.25, 121.52) * mm, "radius": 2.5 * mm});
            skSolve(sketch);
        }
        {
            var Q0;
            Q0=qSketchRegion(id+"F37",true);
            var Q1;
            Q1=makeQuery(id+"F21.opExtrude","SWEPT_BODY",BODY,{"disambiguationData":[OSD([sQuery(id+"F20.wireOp",EDGE,"E39.0"),sQuery(id+"F20.wireOp",EDGE,"E39.1"),sQuery(id+"F20.wireOp",EDGE,"E39.2"),sQuery(id+"F20.wireOp",EDGE,"E39.3"),sQuery(id+"F20.wireOp",EDGE,"E39.4"),sQuery(id+"F20.wireOp",EDGE,"E39.5"),sQuery(id+"F20.wireOp",EDGE,"E39.6"),sQuery(id+"F20.wireOp",EDGE,"E39.7"),sQuery(id+"F20.wireOp",EDGE,"E39.8"),sQuery(id+"F20.wireOp",EDGE,"E39.9"),sQuery(id+"F20.wireOp",EDGE,"E39.10"),sQuery(id+"F20.wireOp",EDGE,"E39.11")])]});
            var Q2;
            Q2=makeQuery(id+"F25.opExtrude","SWEPT_FACE",FACE,{"disambiguationData":[OSD([sQuery(id+"F18.wireOp",EDGE,"E37.0")])]});
            extrude(context, id + "F38", {"entities" : qUnion([Q0]), "operationType" : NewBodyOperationType.ADD, "endBound" : BoundingType.UP_TO_BODY, "oppositeDirection" : true, "depth" : 25 * mm, "endBoundEntityBody" : qUnion([Q1]), "offsetDistance" : 25 * mm, "hasDraft" : true, "draftAngle" : 1 * degree, "hasSecondDirection" : true, "secondDirectionBound" : BoundingType.UP_TO_SURFACE, "secondDirectionOppositeDirection" : true, "secondDirectionDepth" : 25 * mm, "secondDirectionBoundEntityFace" : qUnion([Q2])});
        }
        {
            var Q0;
            Q0=qCreatedBy(makeId("Front.planeOp"),FACE);
            cPlane(context, id + "F39", {"entities" : qUnion([Q0]), "cplaneType" : CPlaneType.OFFSET, "offset" : 25 * mm, "oppositeDirection" : true, "width" : 150 * mm, "height" : 150 * mm});
        }
        {
            var Q0;
            Q0=qCreatedBy(id+"F39.planeOp",FACE);
            var sketch = newSketch(context, id + "F40", { "sketchPlane" : qUnion([Q0])});
            skCircle(sketch, "E61.0", {"center": v(17.25, 112.52) * mm, "radius": 6.5 * mm});
            skCircle(sketch, "E61.1", {"center": v(58.25, 121.52) * mm, "radius": 1.5 * mm});
            skCircle(sketch, "E61.2", {"center": v(50.75, 80.95) * mm, "radius": 4 * mm});
            skCircle(sketch, "E61.3", {"center": v(48.25, 17.25) * mm, "radius": 6.5 * mm});
            skLineSegment(sketch, "E61.4", {"start": v(32.75, -0.52) * mm, "end": v(32.75, 50.45) * mm, "construction": true});
            skCircle(sketch, "E61.5", {"center": v(17.25, 17.25) * mm, "radius": 6.5 * mm});
            skLineSegment(sketch, "E61.6", {"start": v(4.5, -0.52) * mm, "end": v(61, -0.52) * mm, "construction": true});
            skSolve(sketch);
        }
        {
            var Q0;
            Q0=qSketchRegion(id+"F40",true);
            var Q1;
            Q1=makeQuery(id+"F38.opExtrude","CAP_FACE",FACE,{"disambiguationData":[OSD([sQuery(id+"F37.wireOp",EDGE,"E58.MirrorC")]),topologyDisambiguationEdgeConnected([makeQuery(id+"F25.opExtrude","SWEPT_FACE",FACE,{"disambiguationData":[OSD([sQuery(id+"F18.wireOp",EDGE,"E37.0")])]})])],"isStart":false});
            extrude(context, id + "F41", {"entities" : qUnion([Q0]), "operationType" : NewBodyOperationType.REMOVE, "endBound" : BoundingType.UP_TO_SURFACE, "depth" : 25 * mm, "endBoundEntityFace" : qUnion([Q1]), "hasOffset" : true, "offsetDistance" : 1 * mm, "hasDraft" : true, "draftAngle" : 1 * degree, "draftPullDirection" : true});
        }
        {
            var Q0;
            Q0=makeQuery(id+"F23.boolean.opBoolean","INTERSECT",EDGE,{"derivedFrom":[makeQuery(id+"F21.opExtrude","SWEPT_FACE",FACE,{"disambiguationData":[OSD([sQuery(id+"F20.wireOp",EDGE,"E39.0")])]}),makeQuery(id+"F23.opExtrude","SWEPT_FACE",FACE,{"disambiguationData":[OSD([sQuery(id+"F22.wireOp",EDGE,"E42")])]})]});
            fillet(context, id + "F42", {"entities" : qUnion([Q0]), "radius" : .5 * mm, "tangentPropagation" : true, "allowEdgeOverflow" : false});
        }
        {
            var Q0;
            Q0=makeQuery(id+"F35.boolean.opBoolean","COPY",FACE,{"derivedFrom":makeQuery(id+"F35.opExtrude","SWEPT_FACE",FACE,{"disambiguationData":[OSD([sQuery(id+"F20.wireOp",EDGE,"E40.9")])]})});
            var sketch = newSketch(context, id + "F43", { "sketchPlane" : qUnion([Q0])});
            skEllipticalArc(sketch, "E62.0", {"construction": true});
            skLineSegment(sketch, "E63", {"start": v(32.75, 0.15) * mm, "end": v(32.75, 13.43) * mm, "construction": true});
            skArc(sketch, "E64", {"start": v(30.45, 3.05) * mm, "mid": v(32.75, 0.75) * mm, "end": v(35.05, 3.05) * mm, "construction": true});
            skLineSegment(sketch, "E65", {"start": v(30.45, 12.4) * mm, "end": v(35.05, 12.4) * mm});
            skLineSegment(sketch, "E66", {"start": v(30.45, 0.65) * mm, "end": v(35.05, 0.65) * mm});
            skLineSegment(sketch, "E67", {"start": v(30.45, 12.4) * mm, "end": v(30.45, 0.65) * mm});
            skLineSegment(sketch, "E68", {"start": v(35.05, 0.65) * mm, "end": v(35.05, 12.4) * mm});
            const initialGuessF43  = {"E62.0": [0.03275, -0.09596723813539623, 0, -1, 0.09611463872501952, 0.0961, 3.0712954359205873, 3.211889871258989]};
            skSetInitialGuess(sketch, initialGuessF43);
            skSolve(sketch);
        }
        {
            var Q0;
            Q0=qSketchRegion(id+"F43",true);
            extrude(context, id + "F44", {"entities" : qUnion([Q0]), "operationType" : NewBodyOperationType.REMOVE, "oppositeDirection" : true, "depth" : 25 * mm, "offsetDistance" : 25 * mm, "hasSecondDirection" : true, "secondDirectionOppositeDirection" : false, "secondDirectionDepth" : 25 * mm});
        }
    });
